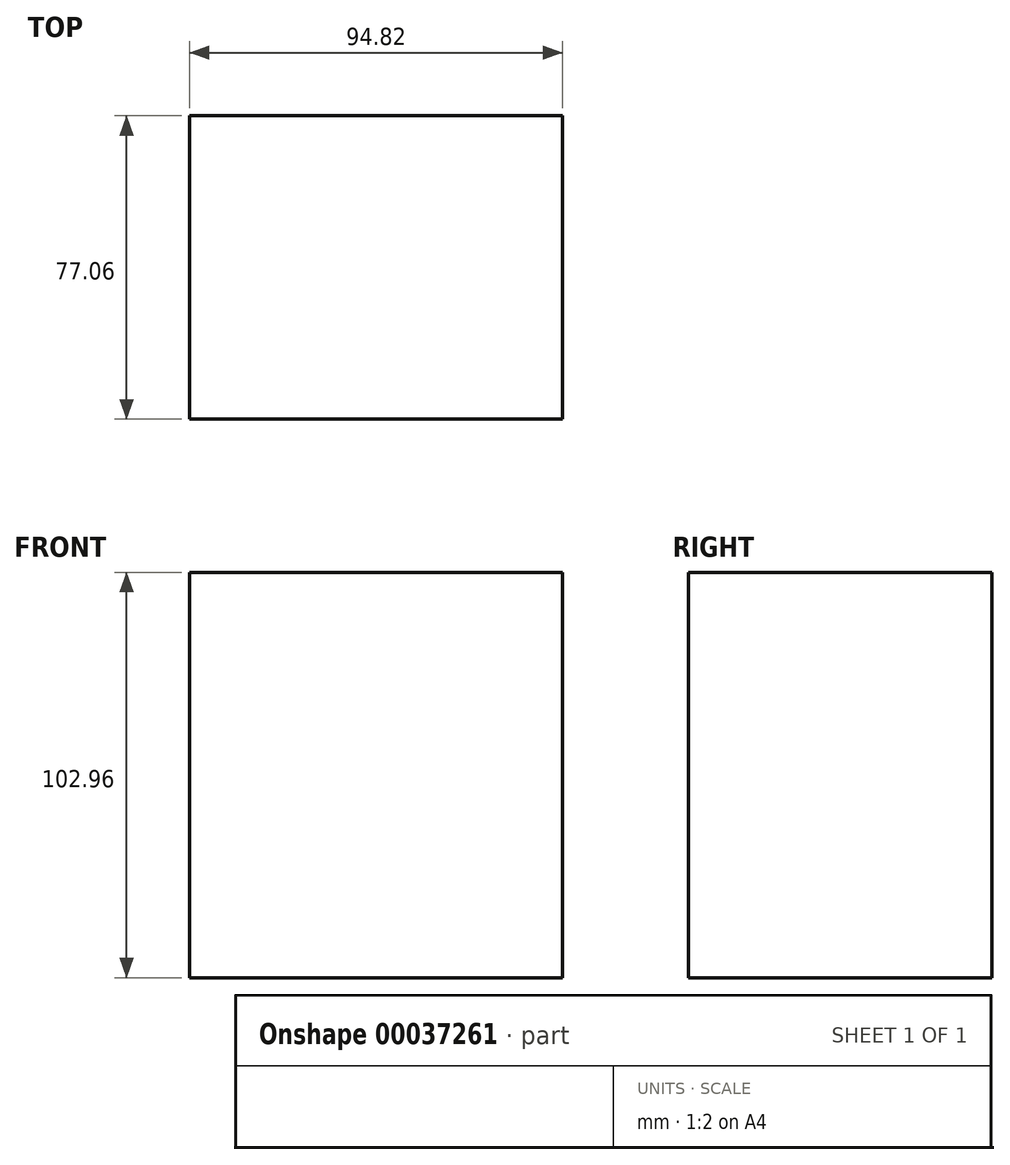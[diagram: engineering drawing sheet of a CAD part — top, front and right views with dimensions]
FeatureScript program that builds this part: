
annotation { "Feature Type Name" : "Feature", "Feature Type Description" : "" }
export const myFeature = defineFeature(function(context is Context, id is Id, definition is map)
    precondition{}
    {
        {
            var Q0;
            Q0=qCreatedBy(makeId("Front.planeOp"),FACE);
            var sketch = newSketch(context, id + "F0", { "sketchPlane" : qUnion([Q0])});
            skLineSegment(sketch, "E0.rect.bottom", {"start": v(47.41, -51.48) * mm, "end": v(-47.41, -51.48) * mm});
            skLineSegment(sketch, "E0.rect.top", {"start": v(47.41, 51.48) * mm, "end": v(-47.41, 51.48) * mm});
            skLineSegment(sketch, "E0.rect.left", {"start": v(47.41, -51.48) * mm, "end": v(47.41, 51.48) * mm});
            skLineSegment(sketch, "E0.rect.right", {"start": v(-47.41, -51.48) * mm, "end": v(-47.41, 51.48) * mm});
            skPoint(sketch, "E0.rect.middle", {"position": v(0, 0) * mm});
            skSolve(sketch);
        }
        {
            var Q0;
            Q0=makeQuery(id+"F0.imprint","IMPRINT",FACE,{"disambiguationData":[TD([[makeQuery(id+"F0.imprint","IMPRINT",EDGE,{"derivedFrom":sQuery(id+"F0.wireOp",EDGE,"E0.rect.bottom")}),-1.0]])]});
            extrude(context, id + "F1", {"entities" : qUnion([Q0]), "depth" : 77.06 * mm});
        }
    });
